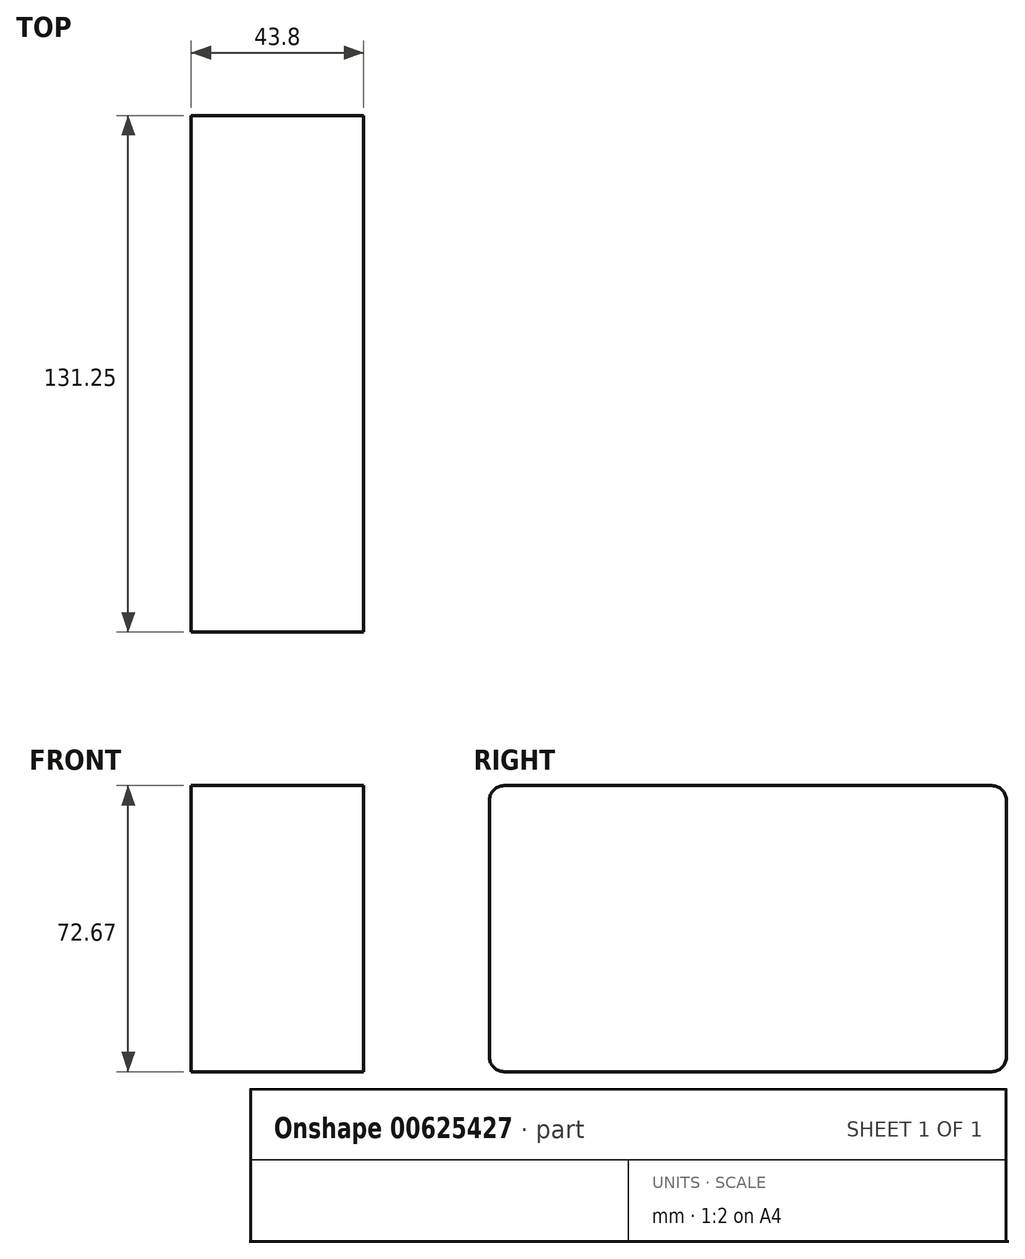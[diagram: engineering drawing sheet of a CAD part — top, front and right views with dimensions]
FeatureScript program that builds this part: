
annotation { "Feature Type Name" : "Feature", "Feature Type Description" : "" }
export const myFeature = defineFeature(function(context is Context, id is Id, definition is map)
    precondition{}
    {
        {
            var Q0;
            Q0=qCreatedBy(makeId("Right.planeOp"),FACE);
            var sketch = newSketch(context, id + "F0", { "sketchPlane" : qUnion([Q0])});
            skLineSegment(sketch, "E0.bottom", {"start": v(-63.97, 37.72) * mm, "end": v(67.28, 37.72) * mm});
            skLineSegment(sketch, "E0.top", {"start": v(-63.97, -34.95) * mm, "end": v(67.28, -34.95) * mm});
            skLineSegment(sketch, "E0.left", {"start": v(-63.97, 37.72) * mm, "end": v(-63.97, -34.95) * mm});
            skLineSegment(sketch, "E0.right", {"start": v(67.28, 37.72) * mm, "end": v(67.28, -34.95) * mm});
            skSolve(sketch);
        }
        {
            var Q0;
            Q0 = qSketchRegion(id + "F0", true);
            extrude(context, id + "F1", {"entities" : qUnion([Q0]), "depth" : 43.8 * mm, "offsetDistance" : 25 * mm});
        }
        {
            var Q0;
            Q0=makeQuery(id+"F1.opExtrude","SWEPT_EDGE",EDGE,{"disambiguationData":[OSD([sQuery(id+"F0.wireOp",EDGE,"E0.top"),sQuery(id+"F0.wireOp",EDGE,"E0.right")])]});
            var Q1;
            Q1=makeQuery(id+"F1.opExtrude","SWEPT_EDGE",EDGE,{"disambiguationData":[OSD([sQuery(id+"F0.wireOp",EDGE,"E0.bottom"),sQuery(id+"F0.wireOp",EDGE,"E0.right")])]});
            var Q2;
            Q2=makeQuery(id+"F1.opExtrude","SWEPT_EDGE",EDGE,{"disambiguationData":[OSD([sQuery(id+"F0.wireOp",EDGE,"E0.top"),sQuery(id+"F0.wireOp",EDGE,"E0.left")])]});
            var Q3;
            Q3=makeQuery(id+"F1.opExtrude","SWEPT_EDGE",EDGE,{"disambiguationData":[OSD([sQuery(id+"F0.wireOp",EDGE,"E0.bottom"),sQuery(id+"F0.wireOp",EDGE,"E0.left")])]});
            fillet(context, id + "F2", {"entities" : qUnion([Q0, Q1, Q2, Q3]), "radius" : 3.62 * mm, "tangentPropagation" : true, "allowEdgeOverflow" : false});
        }
    });
